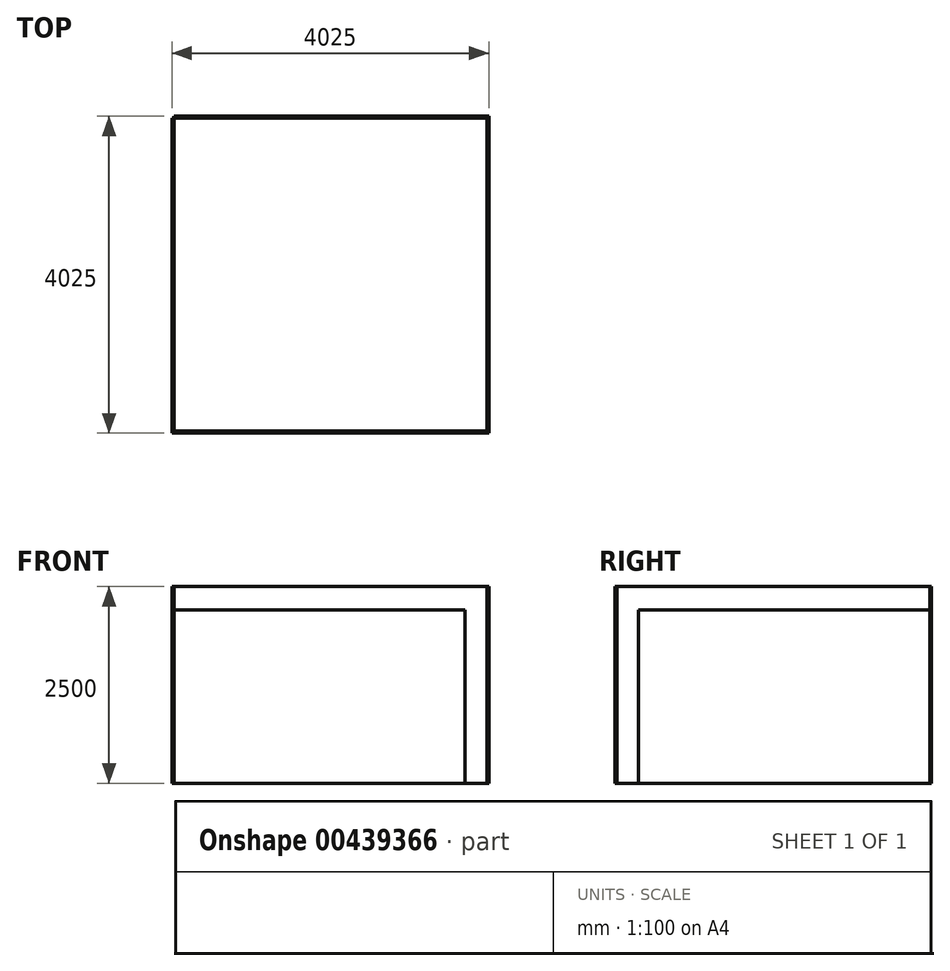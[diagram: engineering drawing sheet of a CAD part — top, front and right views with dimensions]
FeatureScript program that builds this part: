
annotation { "Feature Type Name" : "Feature", "Feature Type Description" : "" }
export const myFeature = defineFeature(function(context is Context, id is Id, definition is map)
    precondition{}
    {
        {
            var Q0;
            Q0=qCreatedBy(makeId("Front.planeOp"),FACE);
            var sketch = newSketch(context, id + "F0", { "sketchPlane" : qUnion([Q0])});
            skLineSegment(sketch, "E0.bottom", {"start": v(0, 0) * mm, "end": v(4000, 0) * mm});
            skLineSegment(sketch, "E0.top", {"start": v(0, 2500) * mm, "end": v(4000, 2500) * mm});
            skLineSegment(sketch, "E0.left", {"start": v(0, 0) * mm, "end": v(0, 2500) * mm});
            skLineSegment(sketch, "E0.right", {"start": v(4000, 0) * mm, "end": v(4000, 2500) * mm});
            skSolve(sketch);
        }
        {
            var Q0;
            Q0=qCreatedBy(makeId("Right.planeOp"),FACE);
            var sketch = newSketch(context, id + "F1", { "sketchPlane" : qUnion([Q0])});
            skLineSegment(sketch, "E1.bottom", {"start": v(0, 0) * mm, "end": v(-4000, 0) * mm});
            skLineSegment(sketch, "E1.top", {"start": v(0, 2500) * mm, "end": v(-4000, 2500) * mm});
            skLineSegment(sketch, "E1.left", {"start": v(0, 0) * mm, "end": v(0, 2500) * mm});
            skLineSegment(sketch, "E1.right", {"start": v(-4000, 0) * mm, "end": v(-4000, 2500) * mm});
            skSolve(sketch);
        }
        {
            var Q0;
            Q0=qCreatedBy(makeId("Top.planeOp"),FACE);
            var sketch = newSketch(context, id + "F2", { "sketchPlane" : qUnion([Q0])});
            skLineSegment(sketch, "E2.bottom", {"start": v(0, 0) * mm, "end": v(4000, 0) * mm});
            skLineSegment(sketch, "E2.top", {"start": v(0, -4000) * mm, "end": v(4000, -4000) * mm});
            skLineSegment(sketch, "E2.left", {"start": v(0, 0) * mm, "end": v(0, -4000) * mm});
            skLineSegment(sketch, "E2.right", {"start": v(4000, 0) * mm, "end": v(4000, -4000) * mm});
            skSolve(sketch);
        }
        {
            var Q0;
            Q0=makeQuery(id+"F2.imprint","IMPRINT",FACE,{"disambiguationData":[TD([[makeQuery(id+"F2.imprint","IMPRINT",EDGE,{"derivedFrom":sQuery(id+"F2.wireOp",EDGE,"E2.bottom")}),-1.0]])]});
            extrude(context, id + "F3", {"entities" : qUnion([Q0]), "depth" : 2 * mm});
        }
        {
            var Q0;
            Q0=makeQuery(id+"F1.imprint","IMPRINT",FACE,{"disambiguationData":[TD([[makeQuery(id+"F1.imprint","IMPRINT",EDGE,{"derivedFrom":sQuery(id+"F1.wireOp",EDGE,"E1.bottom")}),-1.0]])]});
            extrude(context, id + "F4", {"entities" : qUnion([Q0]), "oppositeDirection" : true, "depth" : 25 * mm});
        }
        {
            var Q0;
            Q0=makeQuery(id+"F0.imprint","IMPRINT",FACE,{"disambiguationData":[TD([[makeQuery(id+"F0.imprint","IMPRINT",EDGE,{"derivedFrom":sQuery(id+"F0.wireOp",EDGE,"E0.bottom")}),1.0]])]});
            extrude(context, id + "F5", {"entities" : qUnion([Q0]), "oppositeDirection" : true, "depth" : 25 * mm});
        }
        {
            var Q0;
            Q0=qCreatedBy(makeId("Front.planeOp"),FACE);
            cPlane(context, id + "F6", {"entities" : qUnion([Q0]), "cplaneType" : CPlaneType.OFFSET, "offset" : 4000 * mm, "width" : 150 * mm, "height" : 150 * mm});
        }
        {
            var Q0;
            Q0=qCreatedBy(makeId("Right.planeOp"),FACE);
            cPlane(context, id + "F7", {"entities" : qUnion([Q0]), "cplaneType" : CPlaneType.OFFSET, "offset" : 4000 * mm, "width" : 150 * mm, "height" : 150 * mm});
        }
        {
            var Q0;
            Q0=qCreatedBy(id+"F6.planeOp",FACE);
            var sketch = newSketch(context, id + "F8", { "sketchPlane" : qUnion([Q0])});
            skLineSegment(sketch, "E3.bottom", {"start": v(0, 2500) * mm, "end": v(4000, 2500) * mm});
            skLineSegment(sketch, "E3.top", {"start": v(0, 2200) * mm, "end": v(4000, 2200) * mm});
            skLineSegment(sketch, "E3.left", {"start": v(0, 2500) * mm, "end": v(0, 2200) * mm});
            skLineSegment(sketch, "E3.right", {"start": v(4000, 2500) * mm, "end": v(4000, 2200) * mm});
            skLineSegment(sketch, "E4.bottom", {"start": v(4000, 2500) * mm, "end": v(3700, 2500) * mm});
            skLineSegment(sketch, "E4.top", {"start": v(4000, 0) * mm, "end": v(3700, 0) * mm});
            skLineSegment(sketch, "E4.left", {"start": v(4000, 2500) * mm, "end": v(4000, 0) * mm});
            skLineSegment(sketch, "E4.right", {"start": v(3700, 2500) * mm, "end": v(3700, 0) * mm});
            skSolve(sketch);
        }
        {
            var Q0;
            {var subQ5=sQuery(id+"F8.wireOp",EDGE,"E4.top");Q0=makeQuery(id+"F8.imprint","IMPRINT",FACE,{"disambiguationData":[TD([[makeQuery(id+"F8.imprint","IMPRINT",EDGE,{"derivedFrom":subQ5}),-1.0]])]});}
            var Q1;
            {var subQ5=sQuery(id+"F8.wireOp",EDGE,"E4.bottom");Q1=makeQuery(id+"F8.imprint","IMPRINT",FACE,{"disambiguationData":[TD([[makeQuery(id+"F8.imprint","IMPRINT",EDGE,{"derivedFrom":subQ5}),1.0]])]});}
            var Q2;
            {var subQ0=sQuery(id+"F8.wireOp",EDGE,"E3.bottom");Q2=makeQuery(id+"F8.imprint","IMPRINT",FACE,{"disambiguationData":[TD([[makeQuery(id+"F8.imprint","IMPRINT",EDGE,{"derivedFrom":subQ0}),-1.0]])]});}
            extrude(context, id + "F9", {"entities" : qUnion([Q0, Q1, Q2]), "oppositeDirection" : true, "depth" : 25 * mm});
        }
        {
            var Q0;
            Q0=qCreatedBy(id+"F7.planeOp",FACE);
            var sketch = newSketch(context, id + "F10", { "sketchPlane" : qUnion([Q0])});
            skLineSegment(sketch, "E5.bottom", {"start": v(0, 2200) * mm, "end": v(-4000, 2200) * mm});
            skLineSegment(sketch, "E5.top", {"start": v(0, 2500) * mm, "end": v(-4000, 2500) * mm});
            skLineSegment(sketch, "E5.left", {"start": v(0, 2200) * mm, "end": v(0, 2500) * mm});
            skLineSegment(sketch, "E5.right", {"start": v(-4000, 2200) * mm, "end": v(-4000, 2500) * mm});
            skLineSegment(sketch, "E6.bottom", {"start": v(-4000, 2500) * mm, "end": v(-3700, 2500) * mm});
            skLineSegment(sketch, "E6.top", {"start": v(-4000, 0) * mm, "end": v(-3700, 0) * mm});
            skLineSegment(sketch, "E6.left", {"start": v(-4000, 2500) * mm, "end": v(-4000, 0) * mm});
            skLineSegment(sketch, "E6.right", {"start": v(-3700, 2500) * mm, "end": v(-3700, 0) * mm});
            skSolve(sketch);
        }
        {
            var Q0;
            {var subQ4=sQuery(id+"F10.wireOp",EDGE,"E5.top");Q0=makeQuery(id+"F10.imprint","IMPRINT",FACE,{"disambiguationData":[TD([[makeQuery(id+"F10.imprint","IMPRINT",EDGE,{"derivedFrom":subQ4}),1.0]])]});}
            var Q1;
            {var subQ5=sQuery(id+"F10.wireOp",EDGE,"E6.bottom");Q1=makeQuery(id+"F10.imprint","IMPRINT",FACE,{"disambiguationData":[TD([[makeQuery(id+"F10.imprint","IMPRINT",EDGE,{"derivedFrom":subQ5}),-1.0]])]});}
            var Q2;
            {var subQ5=sQuery(id+"F10.wireOp",EDGE,"E6.top");Q2=makeQuery(id+"F10.imprint","IMPRINT",FACE,{"disambiguationData":[TD([[makeQuery(id+"F10.imprint","IMPRINT",EDGE,{"derivedFrom":subQ5}),1.0]])]});}
            extrude(context, id + "F11", {"entities" : qUnion([Q0, Q1, Q2]), "oppositeDirection" : true, "depth" : 25 * mm});
        }
    });
